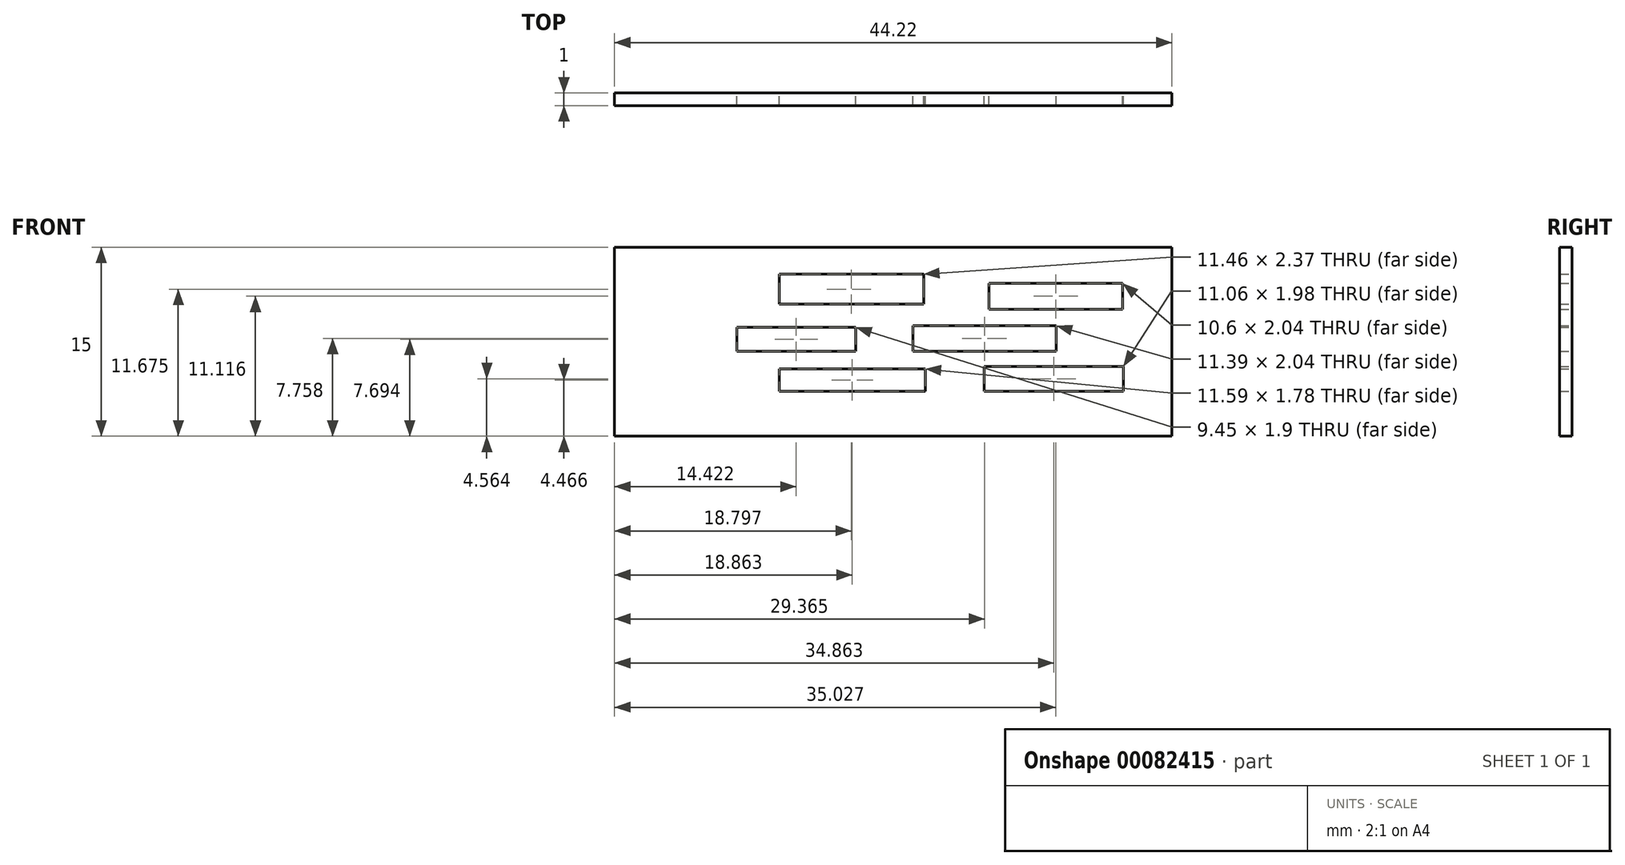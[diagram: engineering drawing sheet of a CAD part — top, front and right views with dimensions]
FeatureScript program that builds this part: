
annotation { "Feature Type Name" : "Feature", "Feature Type Description" : "" }
export const myFeature = defineFeature(function(context is Context, id is Id, definition is map)
    precondition{}
    {
        {
            var Q0;
            Q0=qCreatedBy(makeId("Top.planeOp"),FACE);
            var sketch = newSketch(context, id + "F0", { "sketchPlane" : qUnion([Q0])});
            skCircle(sketch, "E0", {"center": v(0, 0) * mm, "radius": 35 * mm});
            skCircle(sketch, "E1", {"center": v(0, 0) * mm, "radius": 34.25 * mm});
            skSolve(sketch);
        }
        {
            var Q0;
            Q0=makeQuery(id+"F0.imprint","IMPRINT",FACE,{"disambiguationData":[TD([[makeQuery(id+"F0.imprint","IMPRINT",EDGE,{"derivedFrom":sQuery(id+"F0.wireOp",EDGE,"E0")}),1.0]])]});
            extrude(context, id + "F1", {"entities" : qUnion([Q0]), "depth" : 15 * mm});
        }
        {
            var Q0;
            Q0=qCreatedBy(makeId("Top.planeOp"),FACE);
            var sketch = newSketch(context, id + "F2", { "sketchPlane" : qUnion([Q0])});
            skLineSegment(sketch, "E2", {"start": v(1.2, 55.42) * mm, "end": v(45.42, 55.42) * mm});
            skLineSegment(sketch, "E3.0", {"start": v(1.2, 54.42) * mm, "end": v(45.42, 54.42) * mm});
            skLineSegment(sketch, "E4", {"start": v(1.2, 55.42) * mm, "end": v(1.2, 54.42) * mm});
            skLineSegment(sketch, "E5", {"start": v(45.42, 55.42) * mm, "end": v(45.42, 54.42) * mm});
            skSolve(sketch);
        }
        {
            var Q0;
            Q0=makeQuery(id+"F2.imprint","IMPRINT",FACE,{"disambiguationData":[TD([[makeQuery(id+"F2.imprint","IMPRINT",EDGE,{"derivedFrom":sQuery(id+"F2.wireOp",EDGE,"E2")}),-1.0]])]});
            extrude(context, id + "F3", {"entities" : qUnion([Q0]), "depth" : 15 * mm});
        }
        {
            var Q0;
            Q0=makeQuery(id+"F3.opExtrude","SWEPT_FACE",FACE,{"disambiguationData":[OSD([sQuery(id+"F2.wireOp",EDGE,"E2")])]});
            var sketch = newSketch(context, id + "F4", { "sketchPlane" : qUnion([Q0])});
            skLineSegment(sketch, "E6.bottom", {"start": v(-41.53, 12.14) * mm, "end": v(-30.93, 12.14) * mm});
            skLineSegment(sketch, "E6.top", {"start": v(-41.53, 10.1) * mm, "end": v(-30.93, 10.1) * mm});
            skLineSegment(sketch, "E6.left", {"start": v(-41.53, 12.14) * mm, "end": v(-41.53, 10.1) * mm});
            skLineSegment(sketch, "E6.right", {"start": v(-30.93, 12.14) * mm, "end": v(-30.93, 10.1) * mm});
            skLineSegment(sketch, "E7.bottom", {"start": v(-36.26, 8.78) * mm, "end": v(-24.87, 8.78) * mm});
            skLineSegment(sketch, "E7.top", {"start": v(-36.26, 6.74) * mm, "end": v(-24.87, 6.74) * mm});
            skLineSegment(sketch, "E7.left", {"start": v(-36.26, 8.78) * mm, "end": v(-36.26, 6.74) * mm});
            skLineSegment(sketch, "E7.right", {"start": v(-24.87, 8.78) * mm, "end": v(-24.87, 6.74) * mm});
            skLineSegment(sketch, "E8.bottom", {"start": v(-41.6, 5.55) * mm, "end": v(-30.53, 5.55) * mm});
            skLineSegment(sketch, "E8.top", {"start": v(-41.6, 3.58) * mm, "end": v(-30.53, 3.58) * mm});
            skLineSegment(sketch, "E8.left", {"start": v(-41.6, 5.55) * mm, "end": v(-41.6, 3.58) * mm});
            skLineSegment(sketch, "E8.right", {"start": v(-30.53, 5.55) * mm, "end": v(-30.53, 3.58) * mm});
            skLineSegment(sketch, "E9.bottom", {"start": v(-25.86, 5.35) * mm, "end": v(-14.27, 5.35) * mm});
            skLineSegment(sketch, "E9.top", {"start": v(-25.86, 3.58) * mm, "end": v(-14.27, 3.58) * mm});
            skLineSegment(sketch, "E9.left", {"start": v(-25.86, 5.35) * mm, "end": v(-25.86, 3.58) * mm});
            skLineSegment(sketch, "E9.right", {"start": v(-14.27, 5.35) * mm, "end": v(-14.27, 3.58) * mm});
            skLineSegment(sketch, "E10.bottom", {"start": v(-25.73, 12.86) * mm, "end": v(-14.27, 12.86) * mm});
            skLineSegment(sketch, "E10.top", {"start": v(-25.73, 10.5) * mm, "end": v(-14.27, 10.5) * mm});
            skLineSegment(sketch, "E10.left", {"start": v(-25.73, 12.86) * mm, "end": v(-25.73, 10.5) * mm});
            skLineSegment(sketch, "E10.right", {"start": v(-14.27, 12.86) * mm, "end": v(-14.27, 10.5) * mm});
            skLineSegment(sketch, "E11.bottom", {"start": v(-20.35, 8.65) * mm, "end": v(-10.9, 8.65) * mm});
            skLineSegment(sketch, "E11.top", {"start": v(-20.35, 6.74) * mm, "end": v(-10.9, 6.74) * mm});
            skLineSegment(sketch, "E11.left", {"start": v(-20.35, 8.65) * mm, "end": v(-20.35, 6.74) * mm});
            skLineSegment(sketch, "E11.right", {"start": v(-10.9, 8.65) * mm, "end": v(-10.9, 6.74) * mm});
            skSolve(sketch);
        }
        {
            var Q0;
            Q0=makeQuery(id+"F4.imprint","IMPRINT",FACE,{"disambiguationData":[TD([[makeQuery(id+"F4.imprint","IMPRINT",EDGE,{"derivedFrom":sQuery(id+"F4.wireOp",EDGE,"E6.bottom")}),1.0]])]});
            extrude(context, id + "F5", {"entities" : qUnion([Q0]), "operationType" : NewBodyOperationType.INTERSECT, "oppositeDirection" : true, "depth" : 2 * mm});
        }
    });
